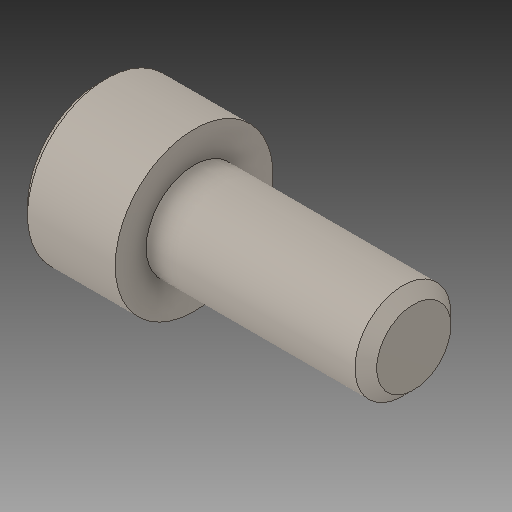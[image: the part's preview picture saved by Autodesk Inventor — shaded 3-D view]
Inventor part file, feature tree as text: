
AUTODESK INVENTOR PART (.ipt)
format: ipt  version: 2019 (Build 230136000, 136)  size: 128,512 bytes
history: native  units: in
note: dims shown in document units (in); Inventor stores cm internally (conversion verified against a paired STEP export)
features: chamfer x1
ambient origin geometry x8: Origin, YZ Plane, XZ Plane, XY Plane, X Axis, Y Axis, Z Axis, Center Point
bodies: Solid1 (feature_tree)
feature tree (1):
  chamfer  "Chamfer1"  [1 undecoded]
note: 1 required parameter value undecoded (feature->parameter linkage not recoverable at this tier; creation-order binding heuristic only, values carry confidence <= 0.55)
